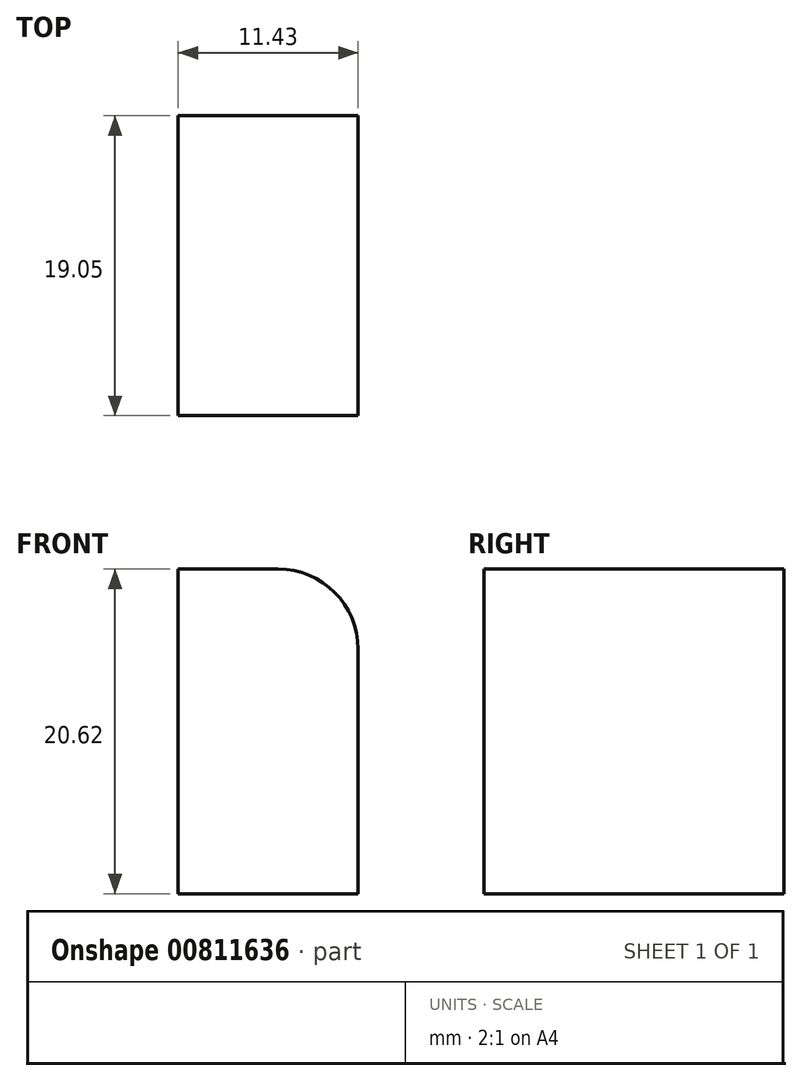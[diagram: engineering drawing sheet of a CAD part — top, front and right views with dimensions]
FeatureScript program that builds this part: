
annotation { "Feature Type Name" : "Feature", "Feature Type Description" : "" }
export const myFeature = defineFeature(function(context is Context, id is Id, definition is map)
    precondition{}
    {
        {
            var Q0;
            Q0=qCreatedBy(makeId("Front.planeOp"),FACE);
            var sketch = newSketch(context, id + "F0", { "sketchPlane" : qUnion([Q0])});
            skLineSegment(sketch, "E0.bottom", {"start": v(0, 0) * mm, "end": v(11.43, 0) * mm});
            skLineSegment(sketch, "E0.top", {"start": v(0, 20.62) * mm, "end": v(11.43, 20.62) * mm});
            skLineSegment(sketch, "E0.left", {"start": v(0, 0) * mm, "end": v(0, 20.62) * mm});
            skLineSegment(sketch, "E0.right", {"start": v(11.43, 0) * mm, "end": v(11.43, 20.62) * mm});
            skPoint(sketch, "E0.middle", {"position": v(5.71, 10.31) * mm});
            skSolve(sketch);
        }
        {
            var Q0;
            Q0 = qSketchRegion(id + "F0", true);
            extrude(context, id + "F1", {"entities" : qUnion([Q0]), "depth" : 19.05 * mm, "offsetDistance" : 25.4 * mm});
        }
        {
            var Q0;
            Q0=makeQuery(id+"F1.opExtrude","SWEPT_EDGE",EDGE,{"disambiguationData":[OSD([sQuery(id+"F0.wireOp",EDGE,"E0.top"),sQuery(id+"F0.wireOp",EDGE,"E0.right")])]});
            fillet(context, id + "F2", {"entities" : qUnion([Q0]), "radius" : 5.08 * mm, "allowEdgeOverflow" : false});
        }
    });
